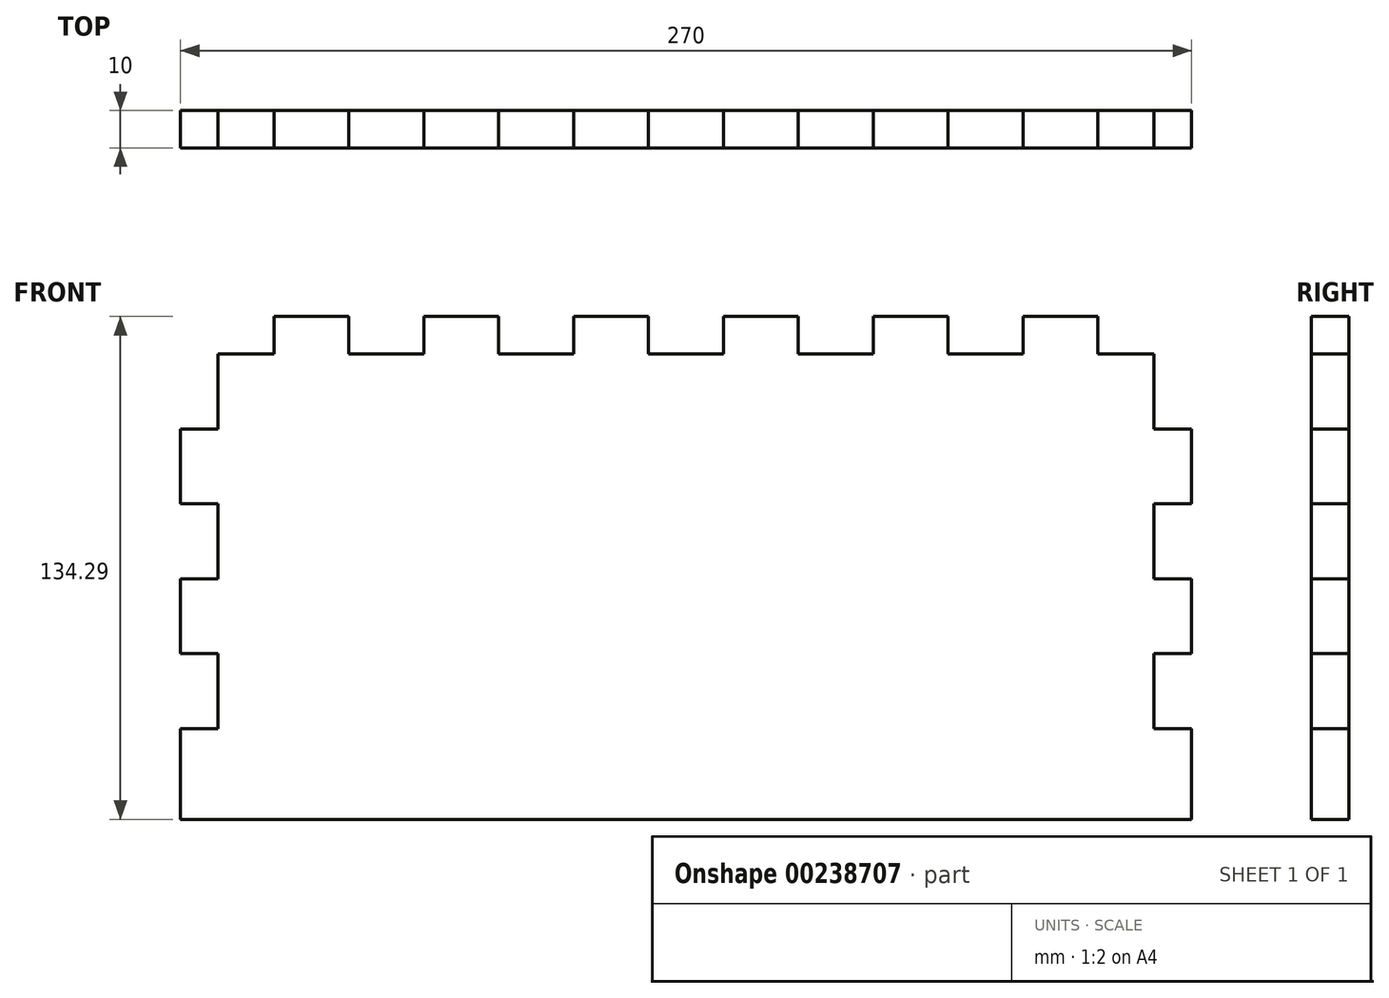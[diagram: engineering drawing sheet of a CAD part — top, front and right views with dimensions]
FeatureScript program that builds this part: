
annotation { "Feature Type Name" : "Feature", "Feature Type Description" : "" }
export const myFeature = defineFeature(function(context is Context, id is Id, definition is map)
    precondition{}
    {
        {
            var Q0;
            Q0=qCreatedBy(makeId("Front.planeOp"),FACE);
            var sketch = newSketch(context, id + "F0", { "sketchPlane" : qUnion([Q0])});
            skLineSegment(sketch, "E0.bottom", {"start": v(0, -100) * mm, "end": v(250, -100) * mm, "construction": true});
            skLineSegment(sketch, "E0.top", {"start": v(0, 40) * mm, "end": v(250, 40) * mm, "construction": true});
            skLineSegment(sketch, "E0.right", {"start": v(250, -100) * mm, "end": v(250, 40) * mm, "construction": true});
            skLineSegment(sketch, "E1", {"start": v(125, -92.5) * mm, "end": v(125, -100) * mm, "construction": true});
            skLineSegment(sketch, "E2.top", {"start": v(135, -110) * mm, "end": v(115, -110) * mm});
            skLineSegment(sketch, "E2.left", {"start": v(135, -100) * mm, "end": v(135, -110) * mm});
            skLineSegment(sketch, "E2.right", {"start": v(115, -100) * mm, "end": v(115, -110) * mm});
            skPoint(sketch, "E2.middle", {"position": v(125, -105) * mm});
            skLineSegment(sketch, "E3", {"start": v(135, -100) * mm, "end": v(155, -100) * mm});
            skLineSegment(sketch, "E4.1.0.0", {"start": v(155, -100) * mm, "end": v(155, -110) * mm});
            skLineSegment(sketch, "E4.1.0.1", {"start": v(175, -110) * mm, "end": v(155, -110) * mm});
            skLineSegment(sketch, "E4.1.0.2", {"start": v(175, -100) * mm, "end": v(175, -110) * mm});
            skLineSegment(sketch, "E4.1.0.3", {"start": v(175, -100) * mm, "end": v(195, -100) * mm});
            skLineSegment(sketch, "E4.2.0.0", {"start": v(195, -100) * mm, "end": v(195, -110) * mm});
            skLineSegment(sketch, "E4.2.0.1", {"start": v(215, -110) * mm, "end": v(195, -110) * mm});
            skLineSegment(sketch, "E4.2.0.2", {"start": v(215, -100) * mm, "end": v(215, -110) * mm});
            skLineSegment(sketch, "E4.2.0.3", {"start": v(215, -100) * mm, "end": v(235, -100) * mm});
            skLineSegment(sketch, "E4.direction1", {"start": v(115, -110) * mm, "end": v(155, -110) * mm, "construction": true});
            skLineSegment(sketch, "E5.0.3.0", {"start": v(235, -100) * mm, "end": v(235, -110) * mm});
            skLineSegment(sketch, "E6.MirrorCS", {"start": v(15, -100) * mm, "end": v(15, -110) * mm});
            skLineSegment(sketch, "E7.MirrorCS", {"start": v(35, -100) * mm, "end": v(35, -110) * mm});
            skLineSegment(sketch, "E8.MirrorCS", {"start": v(35, -110) * mm, "end": v(55, -110) * mm});
            skLineSegment(sketch, "E9.MirrorCS", {"start": v(55, -100) * mm, "end": v(55, -110) * mm});
            skLineSegment(sketch, "E10.MirrorCS", {"start": v(75, -100) * mm, "end": v(75, -110) * mm});
            skLineSegment(sketch, "E11.MirrorCS", {"start": v(75, -110) * mm, "end": v(95, -110) * mm});
            skLineSegment(sketch, "E12.MirrorCS", {"start": v(95, -100) * mm, "end": v(95, -110) * mm});
            skLineSegment(sketch, "E13.MirrorCS", {"start": v(35, -100) * mm, "end": v(15, -100) * mm});
            skLineSegment(sketch, "E14.MirrorCS", {"start": v(115, -100) * mm, "end": v(95, -100) * mm});
            skLineSegment(sketch, "E15.MirrorCS", {"start": v(75, -100) * mm, "end": v(55, -100) * mm});
            skLineSegment(sketch, "E16.bottom", {"start": v(250, -20) * mm, "end": v(260, -20) * mm});
            skLineSegment(sketch, "E16.top", {"start": v(250, -40) * mm, "end": v(260, -40) * mm});
            skLineSegment(sketch, "E16.right", {"start": v(260, -20) * mm, "end": v(260, -40) * mm});
            skPoint(sketch, "E16.middle", {"position": v(255, -30) * mm});
            skPoint(sketch, "E16.middle.positionSnap0", {"position": v(250, -30) * mm});
            skPoint(sketch, "E16.centerSnap0", {"position": v(250, -30) * mm});
            skLineSegment(sketch, "E17", {"start": v(250, -20) * mm, "end": v(250, 0) * mm});
            skLineSegment(sketch, "E18.0.1.0", {"start": v(250, 0) * mm, "end": v(260, 0) * mm});
            skLineSegment(sketch, "E18.0.1.1", {"start": v(260, 20) * mm, "end": v(260, 0) * mm});
            skLineSegment(sketch, "E18.0.1.2", {"start": v(250, 20) * mm, "end": v(260, 20) * mm});
            skLineSegment(sketch, "E18.0.1.3", {"start": v(250, 20) * mm, "end": v(250, 40) * mm});
            skLineSegment(sketch, "E18.0.2.0", {"start": v(250, 40) * mm, "end": v(260, 40) * mm});
            skLineSegment(sketch, "E18.direction1", {"start": v(250, -40) * mm, "end": v(275, -40) * mm, "construction": true});
            skLineSegment(sketch, "E18.direction2", {"start": v(250, -40) * mm, "end": v(250, 0) * mm, "construction": true});
            skLineSegment(sketch, "E19", {"start": v(255, -30) * mm, "end": v(250, -30) * mm, "construction": true});
            skLineSegment(sketch, "E20.MirrorCS", {"start": v(250, -40) * mm, "end": v(250, -60) * mm});
            skLineSegment(sketch, "E21.MirrorCS", {"start": v(250, -60) * mm, "end": v(260, -60) * mm});
            skLineSegment(sketch, "E22.MirrorCS", {"start": v(260, -80) * mm, "end": v(260, -60) * mm});
            skLineSegment(sketch, "E23.MirrorCS", {"start": v(250, -80) * mm, "end": v(260, -80) * mm});
            skLineSegment(sketch, "E24.MirrorCS", {"start": v(250, -80) * mm, "end": v(250, -100) * mm});
            skLineSegment(sketch, "E25.MirrorCS", {"start": v(250, -100) * mm, "end": v(260, -100) * mm});
            skLineSegment(sketch, "E26", {"start": v(235, -110) * mm, "end": v(260, -110) * mm});
            skLineSegment(sketch, "E27", {"start": v(260, -110) * mm, "end": v(260, -100) * mm});
            skLineSegment(sketch, "E28.MirrorCS", {"start": v(35, 40) * mm, "end": v(35, 50) * mm});
            skLineSegment(sketch, "E29.MirrorCS", {"start": v(115, 40) * mm, "end": v(115, 50) * mm});
            skLineSegment(sketch, "E30.MirrorCS", {"start": v(55, 40) * mm, "end": v(55, 50) * mm});
            skLineSegment(sketch, "E31.MirrorCS", {"start": v(155, 40) * mm, "end": v(155, 50) * mm});
            skLineSegment(sketch, "E32.MirrorCS", {"start": v(75, 40) * mm, "end": v(75, 50) * mm});
            skLineSegment(sketch, "E33.MirrorCS", {"start": v(235, 40) * mm, "end": v(235, 50) * mm});
            skLineSegment(sketch, "E34.MirrorCS", {"start": v(95, 40) * mm, "end": v(95, 50) * mm});
            skLineSegment(sketch, "E35.MirrorCS", {"start": v(15, 40) * mm, "end": v(15, 50) * mm});
            skLineSegment(sketch, "E36.MirrorCS", {"start": v(260, 50) * mm, "end": v(260, 40) * mm});
            skLineSegment(sketch, "E37.MirrorCS", {"start": v(175, 40) * mm, "end": v(175, 50) * mm});
            skLineSegment(sketch, "E38.MirrorCS", {"start": v(195, 40) * mm, "end": v(195, 50) * mm});
            skLineSegment(sketch, "E39.MirrorCS", {"start": v(135, 40) * mm, "end": v(135, 50) * mm});
            skLineSegment(sketch, "E40.MirrorCS", {"start": v(215, 40) * mm, "end": v(215, 50) * mm});
            skLineSegment(sketch, "E41.MirrorCS", {"start": v(135, 40) * mm, "end": v(155, 40) * mm});
            skLineSegment(sketch, "E42.MirrorCS", {"start": v(215, 40) * mm, "end": v(235, 40) * mm});
            skLineSegment(sketch, "E43.MirrorCS", {"start": v(175, 40) * mm, "end": v(195, 40) * mm});
            skLineSegment(sketch, "E44.MirrorCS", {"start": v(35, 40) * mm, "end": v(15, 40) * mm});
            skLineSegment(sketch, "E45.MirrorCS", {"start": v(115, 40) * mm, "end": v(95, 40) * mm});
            skLineSegment(sketch, "E46.MirrorCS", {"start": v(75, 40) * mm, "end": v(55, 40) * mm});
            skLineSegment(sketch, "E47.MirrorCS", {"start": v(135, 50) * mm, "end": v(115, 50) * mm});
            skLineSegment(sketch, "E48.MirrorCS", {"start": v(35, 50) * mm, "end": v(55, 50) * mm});
            skLineSegment(sketch, "E49.MirrorCS", {"start": v(175, 50) * mm, "end": v(155, 50) * mm});
            skLineSegment(sketch, "E50.MirrorCS", {"start": v(215, 50) * mm, "end": v(195, 50) * mm});
            skLineSegment(sketch, "E51.MirrorCS", {"start": v(75, 50) * mm, "end": v(95, 50) * mm});
            skLineSegment(sketch, "E52.MirrorCS", {"start": v(235, 50) * mm, "end": v(260, 50) * mm});
            skLineSegment(sketch, "E53.MirrorCS", {"start": v(15, -110) * mm, "end": v(-10, -110) * mm});
            skLineSegment(sketch, "E54.MirrorCS", {"start": v(-10, -110) * mm, "end": v(-10, -100) * mm});
            skLineSegment(sketch, "E55.MirrorCS", {"start": v(0, -100) * mm, "end": v(-10, -100) * mm});
            skLineSegment(sketch, "E56.MirrorCS", {"start": v(0, -80) * mm, "end": v(-10, -80) * mm});
            skLineSegment(sketch, "E57.MirrorCS", {"start": v(-10, -80) * mm, "end": v(-10, -60) * mm});
            skLineSegment(sketch, "E58.MirrorCS", {"start": v(0, -60) * mm, "end": v(-10, -60) * mm});
            skLineSegment(sketch, "E59.MirrorCS", {"start": v(0, -100) * mm, "end": v(0, 40) * mm, "construction": true});
            skLineSegment(sketch, "E60.MirrorCS", {"start": v(-10, -20) * mm, "end": v(-10, -40) * mm, "construction": true});
            skLineSegment(sketch, "E61.MirrorCS", {"start": v(0, -20) * mm, "end": v(-10, -20) * mm});
            skLineSegment(sketch, "E62.MirrorCS", {"start": v(0, 0) * mm, "end": v(-10, 0) * mm});
            skLineSegment(sketch, "E63.MirrorCS", {"start": v(-10, 20) * mm, "end": v(-10, 0) * mm});
            skLineSegment(sketch, "E64.MirrorCS", {"start": v(0, 20) * mm, "end": v(-10, 20) * mm});
            skLineSegment(sketch, "E65.MirrorCS", {"start": v(0, 40) * mm, "end": v(-10, 40) * mm});
            skLineSegment(sketch, "E66.MirrorCS", {"start": v(-10, 50) * mm, "end": v(-10, 40) * mm});
            skLineSegment(sketch, "E67.MirrorCS", {"start": v(0, 20) * mm, "end": v(0, 40) * mm});
            skLineSegment(sketch, "E68.MirrorCS", {"start": v(0, -20) * mm, "end": v(0, 0) * mm});
            skLineSegment(sketch, "E69.MirrorCS", {"start": v(0, -40) * mm, "end": v(0, -60) * mm});
            skLineSegment(sketch, "E70.MirrorCS", {"start": v(0, -80) * mm, "end": v(0, -100) * mm});
            skLineSegment(sketch, "E71.MirrorCS", {"start": v(0, -40) * mm, "end": v(-10, -40) * mm});
            skLineSegment(sketch, "E72", {"start": v(-10, 50) * mm, "end": v(15, 50) * mm});
            skLineSegment(sketch, "E73.bottom", {"start": v(-10, -110) * mm, "end": v(260, -110) * mm, "construction": true});
            skLineSegment(sketch, "E73.top", {"start": v(-10, -234.29) * mm, "end": v(260, -234.29) * mm});
            skLineSegment(sketch, "E73.left", {"start": v(-10, -110) * mm, "end": v(-10, -234.29) * mm, "construction": true});
            skLineSegment(sketch, "E73.right", {"start": v(260, -110) * mm, "end": v(260, -234.29) * mm, "construction": true});
            skLineSegment(sketch, "E74.bottom", {"start": v(260, 50) * mm, "end": v(-10, 50) * mm, "construction": true});
            skLineSegment(sketch, "E74.top", {"start": v(260, 110) * mm, "end": v(-10, 110) * mm});
            skLineSegment(sketch, "E74.left", {"start": v(260, 50) * mm, "end": v(260, 110) * mm, "construction": true});
            skLineSegment(sketch, "E74.right", {"start": v(-10, 50) * mm, "end": v(-10, 110) * mm, "construction": true});
            skLineSegment(sketch, "E75.bottom", {"start": v(260, 40) * mm, "end": v(320, 40) * mm, "construction": true});
            skLineSegment(sketch, "E75.top", {"start": v(260, -100) * mm, "end": v(380, -100) * mm, "construction": true});
            skLineSegment(sketch, "E75.right", {"start": v(320, 40) * mm, "end": v(380, -100) * mm});
            skLineSegment(sketch, "E76.top", {"start": v(260, -110) * mm, "end": v(280, -110) * mm});
            skLineSegment(sketch, "E76.left", {"start": v(260, -100) * mm, "end": v(260, -110) * mm});
            skLineSegment(sketch, "E76.right", {"start": v(280, -100) * mm, "end": v(280, -110) * mm});
            skLineSegment(sketch, "E77", {"start": v(280, -100) * mm, "end": v(300, -100) * mm});
            skLineSegment(sketch, "E78.1.0.0", {"start": v(320, -100) * mm, "end": v(340, -100) * mm});
            skLineSegment(sketch, "E78.1.0.1", {"start": v(320, -100) * mm, "end": v(320, -110) * mm});
            skLineSegment(sketch, "E78.1.0.2", {"start": v(300, -110) * mm, "end": v(320, -110) * mm});
            skLineSegment(sketch, "E78.1.0.3", {"start": v(300, -100) * mm, "end": v(300, -110) * mm});
            skLineSegment(sketch, "E78.2.0.0", {"start": v(360, -100) * mm, "end": v(380, -100) * mm});
            skLineSegment(sketch, "E78.2.0.1", {"start": v(360, -100) * mm, "end": v(360, -110) * mm});
            skLineSegment(sketch, "E78.2.0.2", {"start": v(340, -110) * mm, "end": v(360, -110) * mm});
            skLineSegment(sketch, "E78.2.0.3", {"start": v(340, -100) * mm, "end": v(340, -110) * mm});
            skLineSegment(sketch, "E78.direction1", {"start": v(260, -110) * mm, "end": v(300, -110) * mm, "construction": true});
            skLineSegment(sketch, "E79.top", {"start": v(250, -110) * mm, "end": v(250, -130) * mm});
            skLineSegment(sketch, "E79.left", {"start": v(260, -110) * mm, "end": v(250, -110) * mm});
            skLineSegment(sketch, "E79.right", {"start": v(260, -130) * mm, "end": v(250, -130) * mm});
            skLineSegment(sketch, "E80", {"start": v(260, -130) * mm, "end": v(260, -150) * mm});
            skLineSegment(sketch, "E81.1.0.0", {"start": v(260, -170) * mm, "end": v(260, -190) * mm});
            skLineSegment(sketch, "E81.1.0.1", {"start": v(260, -170) * mm, "end": v(250, -170) * mm});
            skLineSegment(sketch, "E81.1.0.2", {"start": v(250, -150) * mm, "end": v(250, -170) * mm});
            skLineSegment(sketch, "E81.1.0.3", {"start": v(260, -150) * mm, "end": v(250, -150) * mm});
            skLineSegment(sketch, "E81.2.0.1", {"start": v(260, -210) * mm, "end": v(250, -210) * mm});
            skLineSegment(sketch, "E81.2.0.2", {"start": v(250, -190) * mm, "end": v(250, -210) * mm});
            skLineSegment(sketch, "E81.2.0.3", {"start": v(260, -190) * mm, "end": v(250, -190) * mm});
            skLineSegment(sketch, "E81.direction1", {"start": v(250, -110) * mm, "end": v(250, -150) * mm, "construction": true});
            skLineSegment(sketch, "E82.MirrorCS", {"start": v(280, 40) * mm, "end": v(280, 50) * mm});
            skLineSegment(sketch, "E83.MirrorCS", {"start": v(280, 40) * mm, "end": v(300, 40) * mm});
            skLineSegment(sketch, "E84.MirrorCS", {"start": v(300, 40) * mm, "end": v(300, 50) * mm});
            skLineSegment(sketch, "E85.MirrorCS", {"start": v(300, 50) * mm, "end": v(320, 50) * mm});
            skLineSegment(sketch, "E86.MirrorCS", {"start": v(320, 40) * mm, "end": v(320, 50) * mm, "construction": true});
            skLineSegment(sketch, "E87.MirrorCS", {"start": v(260, 40) * mm, "end": v(260, 50) * mm});
            skLineSegment(sketch, "E88.MirrorCS", {"start": v(260, 50) * mm, "end": v(280, 50) * mm});
            skLineSegment(sketch, "E89.MirrorCS", {"start": v(250, 50) * mm, "end": v(250, 70) * mm});
            skLineSegment(sketch, "E90.MirrorCS", {"start": v(260, 70) * mm, "end": v(250, 70) * mm});
            skLineSegment(sketch, "E91.MirrorCS", {"start": v(260, 70) * mm, "end": v(260, 90) * mm});
            skLineSegment(sketch, "E92.MirrorCS", {"start": v(260, 90) * mm, "end": v(250, 90) * mm});
            skLineSegment(sketch, "E93.MirrorCS", {"start": v(250, 90) * mm, "end": v(250, 110) * mm});
            skLineSegment(sketch, "E94.MirrorCS", {"start": v(-10, -210) * mm, "end": v(-10, -234.29) * mm});
            skLineSegment(sketch, "E95.MirrorCS", {"start": v(-10, -210) * mm, "end": v(0, -210) * mm});
            skLineSegment(sketch, "E96.MirrorCS", {"start": v(0, -190) * mm, "end": v(0, -210) * mm});
            skLineSegment(sketch, "E97.MirrorCS", {"start": v(-10, -190) * mm, "end": v(0, -190) * mm});
            skLineSegment(sketch, "E98.MirrorCS", {"start": v(-10, -170) * mm, "end": v(-10, -190) * mm});
            skLineSegment(sketch, "E99.MirrorCS", {"start": v(-10, -170) * mm, "end": v(0, -170) * mm});
            skLineSegment(sketch, "E100.MirrorCS", {"start": v(0, -150) * mm, "end": v(0, -170) * mm});
            skLineSegment(sketch, "E101.MirrorCS", {"start": v(-10, -150) * mm, "end": v(0, -150) * mm});
            skLineSegment(sketch, "E102.MirrorCS", {"start": v(-10, -130) * mm, "end": v(-10, -150) * mm});
            skLineSegment(sketch, "E103.MirrorCS", {"start": v(-10, -130) * mm, "end": v(0, -130) * mm});
            skLineSegment(sketch, "E104.MirrorCS", {"start": v(0, -110) * mm, "end": v(0, -150) * mm, "construction": true});
            skLineSegment(sketch, "E105.MirrorCS", {"start": v(0, -110) * mm, "end": v(0, -130) * mm});
            skLineSegment(sketch, "E106.MirrorCS", {"start": v(0, 50) * mm, "end": v(0, 70) * mm});
            skLineSegment(sketch, "E107.MirrorCS", {"start": v(-10, 70) * mm, "end": v(0, 70) * mm});
            skLineSegment(sketch, "E108.MirrorCS", {"start": v(-10, 70) * mm, "end": v(-10, 90) * mm});
            skLineSegment(sketch, "E109.MirrorCS", {"start": v(-10, 90) * mm, "end": v(0, 90) * mm});
            skLineSegment(sketch, "E110.MirrorCS", {"start": v(0, 90) * mm, "end": v(0, 110) * mm});
            skLineSegment(sketch, "E111", {"start": v(320, 40) * mm, "end": v(315.71, 50) * mm});
            skLineSegment(sketch, "E112", {"start": v(380, -100) * mm, "end": v(384.29, -110) * mm, "construction": true});
            skLineSegment(sketch, "E113", {"start": v(384.29, -110) * mm, "end": v(360, -110) * mm, "construction": true});
            skLineSegment(sketch, "E114", {"start": v(260, -210) * mm, "end": v(260, -234.29) * mm});
            skSolve(sketch);
        }
        {
            var Q0;
            Q0=makeQuery(id+"F0.imprint","IMPRINT",FACE,{"disambiguationData":[TD([[makeQuery(id+"F0.imprint","IMPRINT",EDGE,{"derivedFrom":sQuery(id+"F0.wireOp",EDGE,"6DD6EAd9-EjR4-M54x-3Gs5-ZzkpjLEBHBt8.bottom")}),1.0]])]});
            var Q1;
            Q1=makeQuery(id+"F0.imprint","IMPRINT",FACE,{"disambiguationData":[TD([[makeQuery(id+"F0.imprint","IMPRINT",EDGE,{"derivedFrom":sQuery(id+"F0.wireOp",EDGE,"3aa721ca-eb7f-4933-b860-b67e4f9833b7.bottom")}),1.0]])]});
            var Q2;
            Q2=makeQuery(id+"F0.imprint","IMPRINT",FACE,{"disambiguationData":[TD([[makeQuery(id+"F0.imprint","IMPRINT",EDGE,{"derivedFrom":sQuery(id+"F0.wireOp",EDGE,"1f1aca45-ddc4-4c07-b0ce-2f99aba2689f.bottom")}),1.0]])]});
            var Q3;
            Q3=makeQuery(id+"F0.imprint","IMPRINT",FACE,{"disambiguationData":[TD([[makeQuery(id+"F0.imprint","IMPRINT",EDGE,{"derivedFrom":sQuery(id+"F0.wireOp",EDGE,"cb640f68-ba69-4848-84fb-c352f3b5514c.1.0.0")}),-1.0]])]});
            var Q4;
            Q4=makeQuery(id+"F0.imprint","IMPRINT",FACE,{"disambiguationData":[TD([[makeQuery(id+"F0.imprint","IMPRINT",EDGE,{"derivedFrom":sQuery(id+"F0.wireOp",EDGE,"be0e698b-39bb-4470-8cd3-9eb53d7fa9ec.3.0.4")}),-1.0]])]});
            var Q5;
            Q5=makeQuery(id+"F0.imprint","IMPRINT",FACE,{"disambiguationData":[TD([[makeQuery(id+"F0.imprint","IMPRINT",EDGE,{"derivedFrom":sQuery(id+"F0.wireOp",EDGE,"be0e698b-39bb-4470-8cd3-9eb53d7fa9ec.2.0.4")}),-1.0]])]});
            var Q6;
            Q6=makeQuery(id+"F0.imprint","IMPRINT",FACE,{"disambiguationData":[TD([[makeQuery(id+"F0.imprint","IMPRINT",EDGE,{"derivedFrom":sQuery(id+"F0.wireOp",EDGE,"be0e698b-39bb-4470-8cd3-9eb53d7fa9ec.1.0.4")}),-1.0]])]});
            var Q7;
            Q7=makeQuery(id+"F0.imprint","IMPRINT",FACE,{"disambiguationData":[TD([[makeQuery(id+"F0.imprint","IMPRINT",EDGE,{"derivedFrom":sQuery(id+"F0.wireOp",EDGE,"KLXXNCfZ-N2lI-LQPs-WN5Q-R0OJi47yWmJK")}),-1.0]])]});
            var Q8;
            Q8=makeQuery(id+"F0.imprint","IMPRINT",FACE,{"disambiguationData":[TD([[makeQuery(id+"F0.imprint","IMPRINT",EDGE,{"derivedFrom":sQuery(id+"F0.wireOp",EDGE,"E2.top")}),1.0]])]});
            extrude(context, id + "F1", {"entities" : qUnion([Q0, Q1, Q2, Q3, Q4, Q5, Q6, Q7, Q8]), "oppositeDirection" : true, "depth" : 10 * mm});
        }
    });
